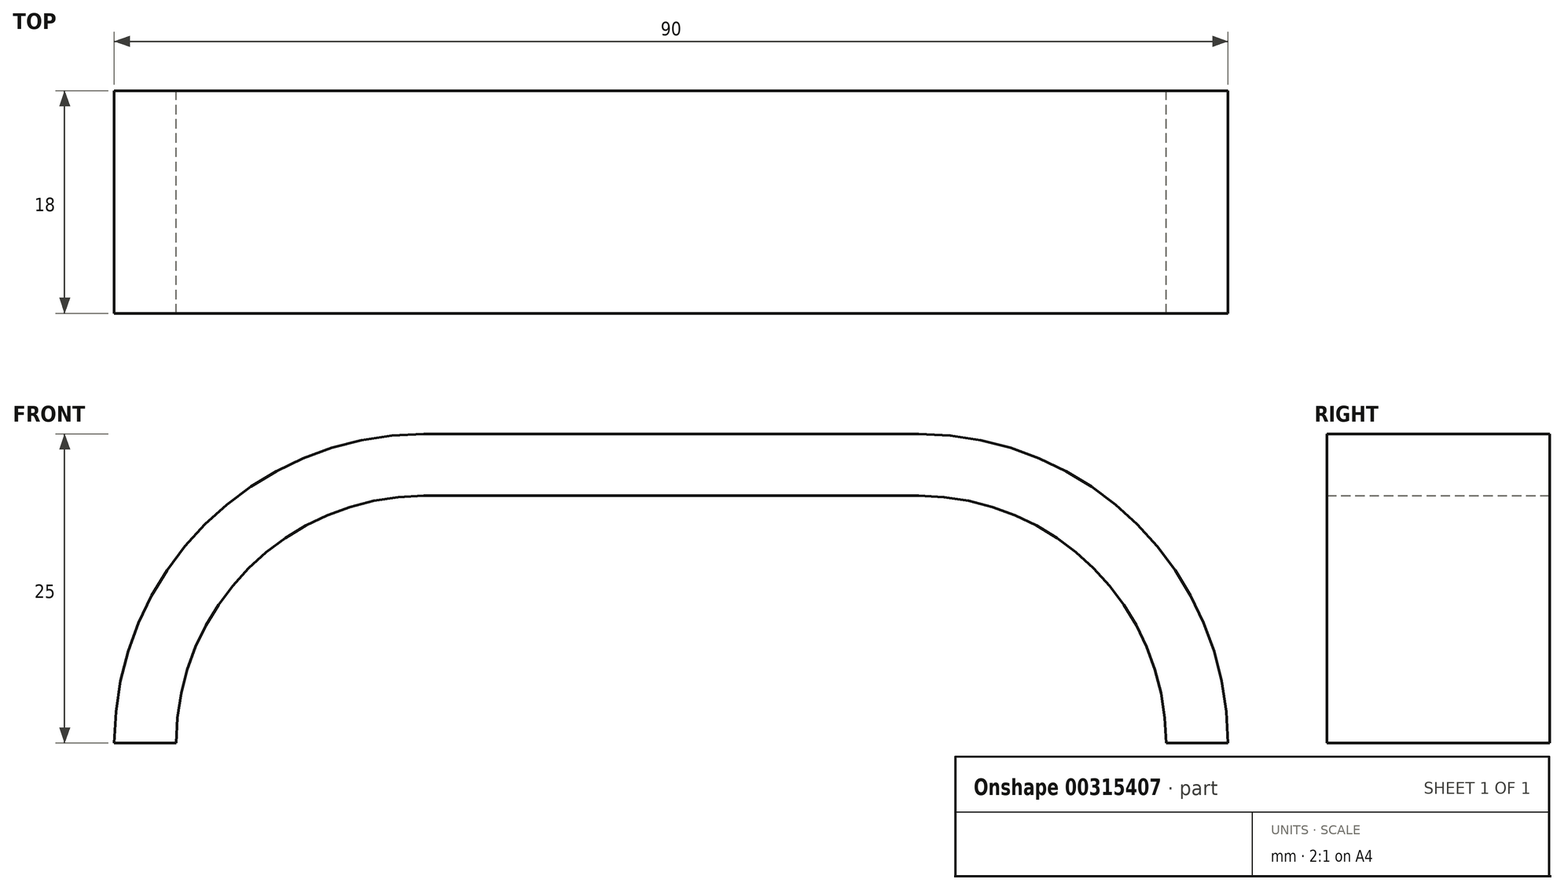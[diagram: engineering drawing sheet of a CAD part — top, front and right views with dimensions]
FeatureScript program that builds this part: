
annotation { "Feature Type Name" : "Feature", "Feature Type Description" : "" }
export const myFeature = defineFeature(function(context is Context, id is Id, definition is map)
    precondition{}
    {
        {
            var Q0;
            Q0=qCreatedBy(makeId("Front.planeOp"),FACE);
            var sketch = newSketch(context, id + "F0", { "sketchPlane" : qUnion([Q0])});
            skCircle(sketch, "E0", {"center": v(-22.49, 0) * mm, "radius": 18.5 * mm, "construction": true});
            skCircle(sketch, "E1", {"center": v(17.51, 0) * mm, "radius": 18.5 * mm, "construction": true});
            skArc(sketch, "E2", {"start": v(-22.49, 20) * mm, "mid": v(-36.63, 14.14) * mm, "end": v(-42.49, 0) * mm});
            skCircle(sketch, "E3", {"center": v(17.51, 0) * mm, "radius": 20 * mm});
            skLineSegment(sketch, "E4.bottom", {"start": v(-22.49, 0) * mm, "end": v(17.51, 0) * mm});
            skLineSegment(sketch, "E4.top", {"start": v(-22.49, 20) * mm, "end": v(-2.49, 20) * mm});
            skLineSegment(sketch, "E4.left", {"start": v(-22.49, 0) * mm, "end": v(-22.49, 20) * mm});
            skPoint(sketch, "E5", {"position": v(-2.49, 0) * mm});
            skPoint(sketch, "E6", {"position": v(0.06, -0.04) * mm});
            skLineSegment(sketch, "E7.bottom", {"start": v(-42.49, 0) * mm, "end": v(31.1, 0) * mm});
            skLineSegment(sketch, "E7.top", {"start": v(-22.49, 25) * mm, "end": v(-2.49, 25) * mm});
            skArc(sketch, "E8", {"start": v(-47.49, 0) * mm, "mid": v(-40.17, 17.68) * mm, "end": v(-22.49, 25) * mm});
            skLineSegment(sketch, "E9", {"start": v(-47.49, 0) * mm, "end": v(-42.49, 0) * mm});
            skLineSegment(sketch, "E10", {"start": v(-2.49, 0) * mm, "end": v(-2.49, 32.93) * mm, "construction": true});
            skLineSegment(sketch, "E11.MirrorCS", {"start": v(17.51, 20) * mm, "end": v(-2.49, 20) * mm});
            skLineSegment(sketch, "E12.MirrorCS", {"start": v(17.51, 25) * mm, "end": v(-2.49, 25) * mm});
            skArc(sketch, "E13.MirrorCS", {"start": v(42.51, 0) * mm, "mid": v(35.19, 17.68) * mm, "end": v(17.51, 25) * mm});
            skLineSegment(sketch, "E14.MirrorCS", {"start": v(42.51, 0) * mm, "end": v(37.51, 0) * mm});
            skArc(sketch, "E15.MirrorC", {"start": v(17.51, 20) * mm, "mid": v(31.65, 14.14) * mm, "end": v(37.51, 0) * mm});
            skSolve(sketch);
        }
        {
            var Q0;
            Q0=makeQuery(id+"F0.imprint","IMPRINT",FACE,{"disambiguationData":[TD([[makeQuery(id+"F0.imprint","IMPRINT",EDGE,{"derivedFrom":sQuery(id+"F0.wireOp",EDGE,"E2")}),-1.0]])]});
            extrude(context, id + "F1", {"entities" : qUnion([Q0]), "depth" : 18 * mm});
        }
    });
